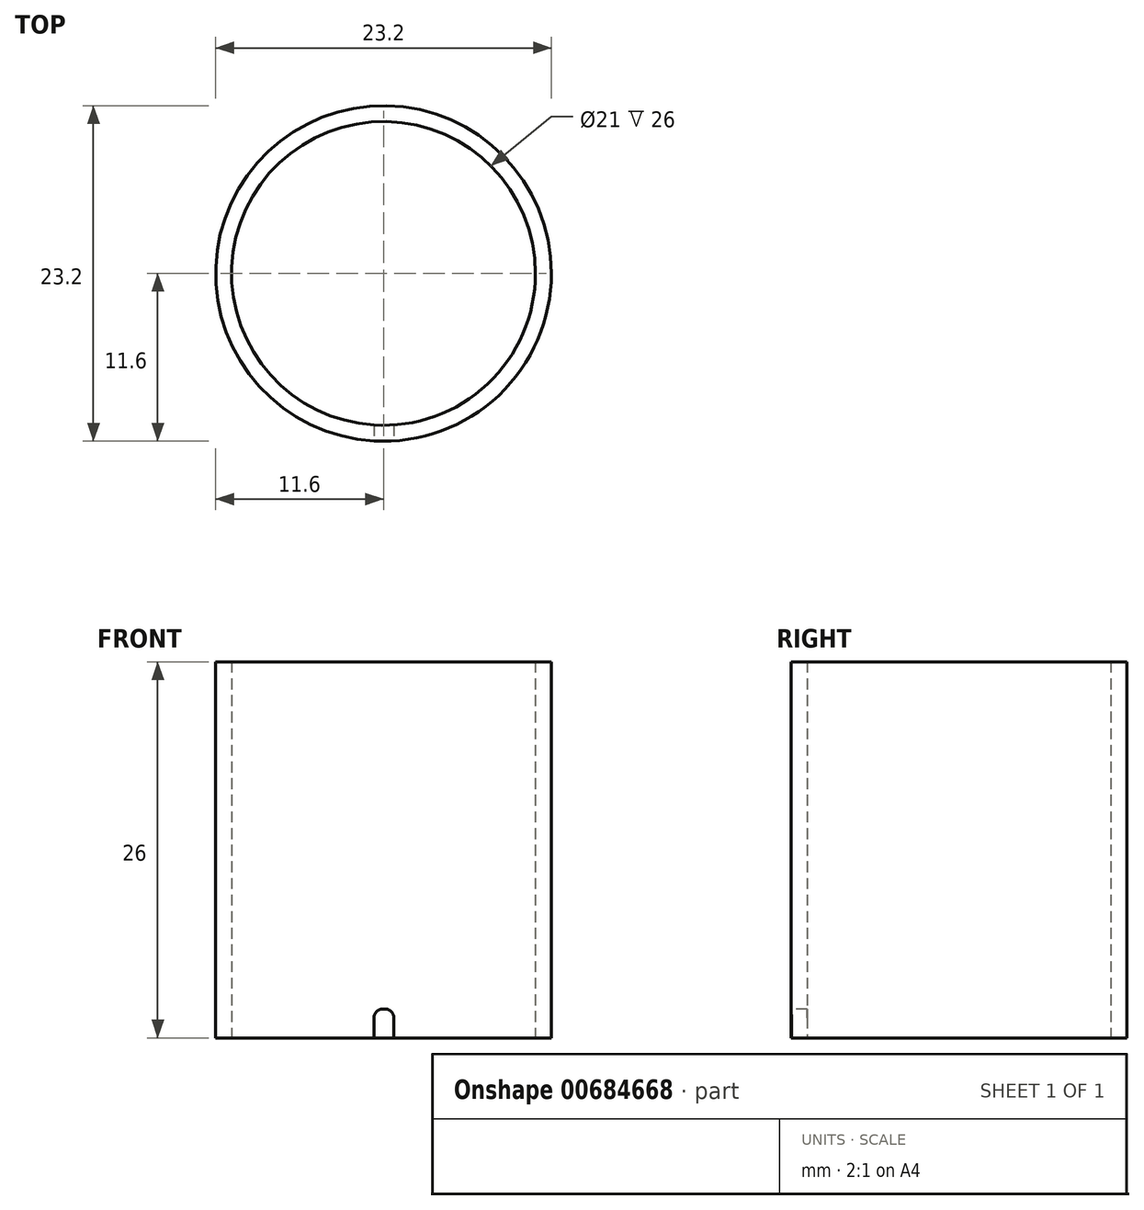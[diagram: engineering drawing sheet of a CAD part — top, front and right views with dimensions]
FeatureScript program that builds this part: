
annotation { "Feature Type Name" : "Feature", "Feature Type Description" : "" }
export const myFeature = defineFeature(function(context is Context, id is Id, definition is map)
    precondition{}
    {
        {
            var Q0;
            Q0=qCreatedBy(makeId("Top.planeOp"),FACE);
            var sketch = newSketch(context, id + "F0", { "sketchPlane" : qUnion([Q0])});
            skCircle(sketch, "E0", {"center": v(0, 0) * mm, "radius": 10.5 * mm});
            skCircle(sketch, "E1", {"center": v(0, 0) * mm, "radius": 11.6 * mm});
            skLineSegment(sketch, "E2.bottom", {"start": v(-0.66, -9.28) * mm, "end": v(0.71, -9.28) * mm});
            skLineSegment(sketch, "E2.top", {"start": v(-0.66, -13.2) * mm, "end": v(0.71, -13.2) * mm});
            skLineSegment(sketch, "E2.left", {"start": v(-0.66, -9.28) * mm, "end": v(-0.66, -13.2) * mm});
            skLineSegment(sketch, "E2.right", {"start": v(0.71, -9.28) * mm, "end": v(0.71, -13.2) * mm});
            skSolve(sketch);
        }
        {
            var Q0;
            {var subQ0=sQuery(id+"F0.wireOp",EDGE,"E2.left");var subQ1=sQuery(id+"F0.wireOp",EDGE,"E0");var subQ2=makeQuery(id+"F0.imprint","INTERSECT",VERTEX,{"derivedFrom":[subQ1,subQ0]});Q0=makeQuery(id+"F0.imprint","IMPRINT",FACE,{"disambiguationData":[TD([[makeQuery(id+"F0.imprint","IMPRINT",EDGE,{"disambiguationData":[TD([[subQ2,1.0]])],"derivedFrom":subQ1}),-1.0]])]});}
            var Q1;
            {var subQ0=sQuery(id+"F0.wireOp",EDGE,"E2.left");var subQ1=sQuery(id+"F0.wireOp",EDGE,"E0");var subQ2=makeQuery(id+"F0.imprint","INTERSECT",VERTEX,{"derivedFrom":[subQ1,subQ0]});Q1=makeQuery(id+"F0.imprint","IMPRINT",FACE,{"disambiguationData":[TD([[makeQuery(id+"F0.imprint","IMPRINT",EDGE,{"disambiguationData":[TD([[subQ2,-1.0]])],"derivedFrom":subQ1}),-1.0]])]});}
            extrude(context, id + "F1", {"entities" : qUnion([Q0, Q1]), "depth" : 26 * mm, "offsetDistance" : 25 * mm});
        }
        {
            var Q0;
            {var subQ0=sQuery(id+"F0.wireOp",EDGE,"E2.left");var subQ1=sQuery(id+"F0.wireOp",EDGE,"E0");var subQ2=makeQuery(id+"F0.imprint","INTERSECT",VERTEX,{"derivedFrom":[subQ1,subQ0]});Q0=makeQuery(id+"F0.imprint","IMPRINT",FACE,{"disambiguationData":[TD([[makeQuery(id+"F0.imprint","IMPRINT",EDGE,{"disambiguationData":[TD([[subQ2,-1.0]])],"derivedFrom":subQ1}),-1.0]])]});}
            extrude(context, id + "F2", {"entities" : qUnion([Q0]), "operationType" : NewBodyOperationType.REMOVE, "depth" : 2 * mm, "offsetDistance" : 25 * mm});
        }
        {
            var Q0;
            Q0=makeQuery(id+"F2.boolean.opBoolean","COPY",EDGE,{"derivedFrom":makeQuery(id+"F2.opExtrude","CAP_EDGE",EDGE,{"disambiguationData":[OSD([sQuery(id+"F0.wireOp",EDGE,"E2.right")])],"isStart":false})});
            var Q1;
            Q1=makeQuery(id+"F2.boolean.opBoolean","COPY",EDGE,{"derivedFrom":makeQuery(id+"F2.opExtrude","CAP_EDGE",EDGE,{"disambiguationData":[OSD([sQuery(id+"F0.wireOp",EDGE,"E2.left")])],"isStart":false})});
            fillet(context, id + "F3", {"entities" : qUnion([Q0, Q1]), "radius" : 0.6 * mm, "tangentPropagation" : true, "allowEdgeOverflow" : false});
        }
    });
